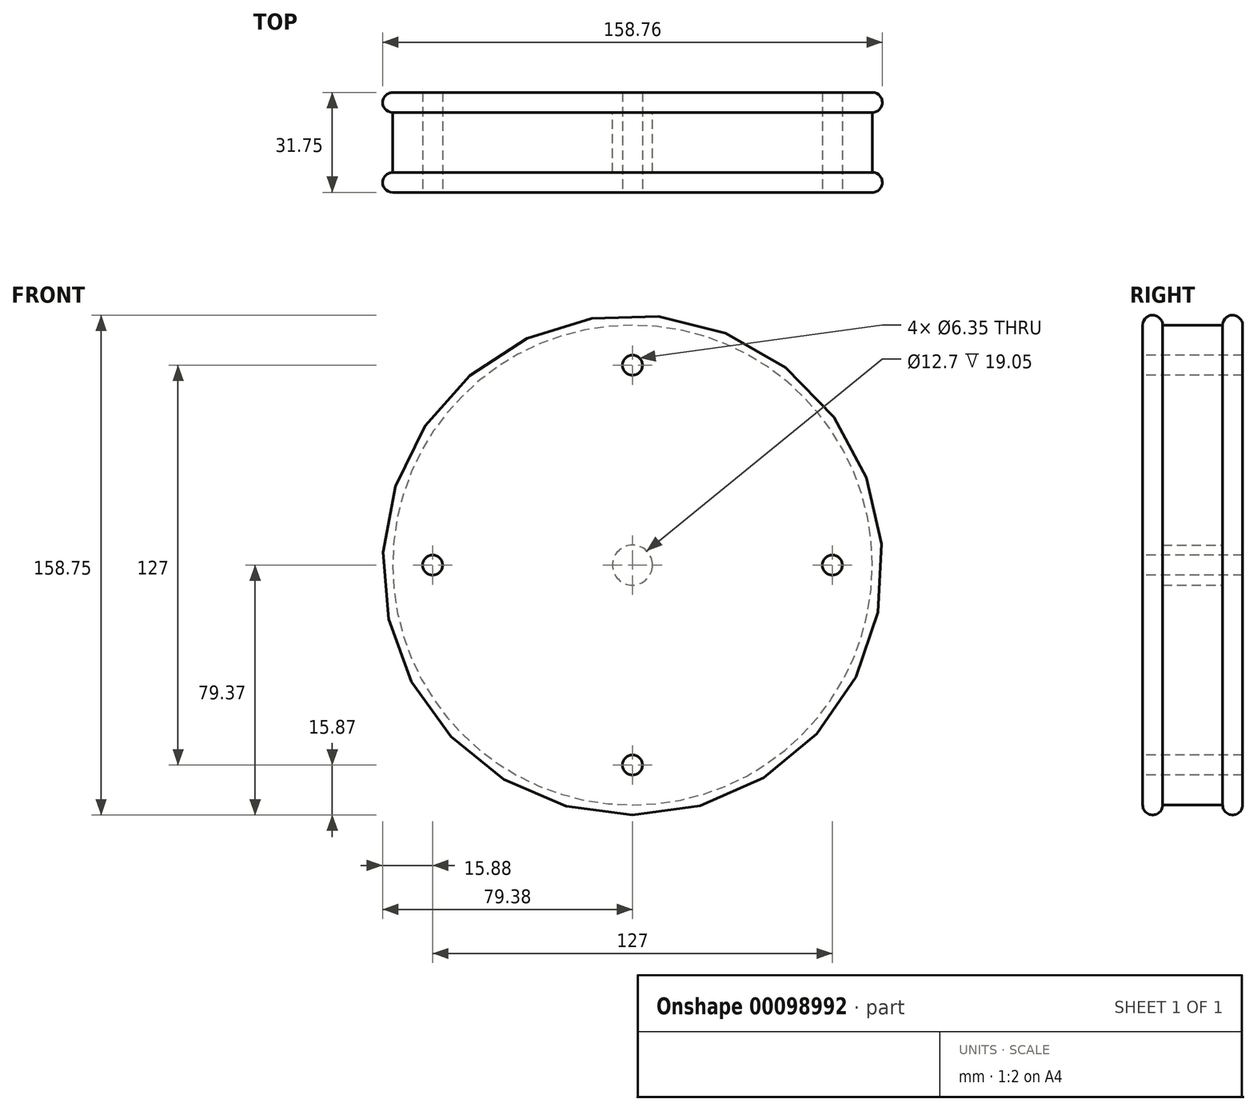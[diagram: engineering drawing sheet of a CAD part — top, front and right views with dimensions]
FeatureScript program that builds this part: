
annotation { "Feature Type Name" : "Feature", "Feature Type Description" : "" }
export const myFeature = defineFeature(function(context is Context, id is Id, definition is map)
    precondition{}
    {
        {
            var Q0;
            Q0=qCreatedBy(makeId("Front.planeOp"),FACE);
            var sketch = newSketch(context, id + "F0", { "sketchPlane" : qUnion([Q0])});
            skCircle(sketch, "E0", {"center": v(0, 0) * mm, "radius": 76.2 * mm});
            skCircle(sketch, "E1", {"center": v(0, 0) * mm, "radius": 6.35 * mm});
            skSolve(sketch);
        }
        {
            var Q0;
            Q0=makeQuery(id+"F0.imprint","IMPRINT",FACE,{"disambiguationData":[TD([[makeQuery(id+"F0.imprint","IMPRINT",EDGE,{"derivedFrom":sQuery(id+"F0.wireOp",EDGE,"E0")}),1.0]])]});
            extrude(context, id + "F1", {"entities" : qUnion([Q0]), "depth" : 25.4 * mm});
        }
        {
            var Q0;
            Q0=makeQuery(id+"F1.opExtrude","CAP_FACE",FACE,{"disambiguationData":[OSD([sQuery(id+"F0.wireOp",EDGE,"E0"),sQuery(id+"F0.wireOp",EDGE,"E1")])],"isStart":false});
            var sketch = newSketch(context, id + "F2", { "sketchPlane" : qUnion([Q0])});
            skCircle(sketch, "E2", {"center": v(0, 0) * mm, "radius": 79.38 * mm});
            skSolve(sketch);
        }
        {
            var Q0;
            Q0 = qSketchRegion(id + "F2", true);
            extrude(context, id + "F3", {"entities" : qUnion([Q0]), "operationType" : NewBodyOperationType.ADD, "oppositeDirection" : true, "depth" : 6.35 * mm});
        }
        {
            var Q0;
            Q0=makeQuery(id+"F0.imprint","IMPRINT",FACE,{"disambiguationData":[TD([[makeQuery(id+"F0.imprint","IMPRINT",EDGE,{"derivedFrom":sQuery(id+"F0.wireOp",EDGE,"E0")}),1.0]])]});
            var sketch = newSketch(context, id + "F4", { "sketchPlane" : qUnion([Q0])});
            skCircle(sketch, "E3", {"center": v(0, 0) * mm, "radius": 79.38 * mm});
            skSolve(sketch);
        }
        {
            var Q0;
            Q0 = qSketchRegion(id + "F4", true);
            extrude(context, id + "F5", {"entities" : qUnion([Q0]), "operationType" : NewBodyOperationType.ADD, "oppositeDirection" : true, "depth" : 6.35 * mm});
        }
        {
            var Q0;
            Q0=makeQuery(id+"F5.opExtrude","CAP_EDGE",EDGE,{"disambiguationData":[OSD([sQuery(id+"F4.wireOp",EDGE,"E3")])],"isStart":false});
            var Q1;
            Q1=makeQuery(id+"F5.opExtrude","CAP_EDGE",EDGE,{"disambiguationData":[OSD([sQuery(id+"F4.wireOp",EDGE,"E3")])],"isStart":true});
            var Q2;
            Q2=makeQuery(id+"F3.opExtrude","CAP_EDGE",EDGE,{"disambiguationData":[OSD([sQuery(id+"F2.wireOp",EDGE,"E2")])],"isStart":false});
            var Q3;
            Q3=makeQuery(id+"F3.opExtrude","CAP_EDGE",EDGE,{"disambiguationData":[OSD([sQuery(id+"F2.wireOp",EDGE,"E2")])],"isStart":true});
            fillet(context, id + "F6", {"entities" : qUnion([Q0, Q1, Q2, Q3]), "radius" : 3.17 * mm, "tangentPropagation" : true, "allowEdgeOverflow" : false});
        }
        {
            var Q0;
            Q0=makeQuery(id+"F3.boolean.opBoolean","MERGE",FACE,{"derivedFrom":[makeQuery(id+"F1.opExtrude","CAP_FACE",FACE,{"disambiguationData":[OSD([sQuery(id+"F0.wireOp",EDGE,"E0"),sQuery(id+"F0.wireOp",EDGE,"E1")])],"isStart":false}),makeQuery(id+"F3.opExtrude","CAP_FACE",FACE,{"disambiguationData":[OSD([sQuery(id+"F2.wireOp",EDGE,"E2")])],"isStart":true})]});
            var sketch = newSketch(context, id + "F7", { "sketchPlane" : qUnion([Q0])});
            skPoint(sketch, "E4", {"position": v(0, 63.5) * mm});
            skPoint(sketch, "E5", {"position": v(0, -63.5) * mm});
            skPoint(sketch, "E6", {"position": v(-63.5, 0) * mm});
            skPoint(sketch, "E7", {"position": v(63.5, 0) * mm});
            skSolve(sketch);
        }
        {
            var Q0;
            Q0=sQuery(id+"F7.wireOp",VERTEX,"E4");
            var Q1;
            Q1=sQuery(id+"F7.wireOp",VERTEX,"E5");
            var Q2;
            Q2=sQuery(id+"F7.wireOp",VERTEX,"E6");
            var Q3;
            Q3=sQuery(id+"F7.wireOp",VERTEX,"E7");
            var Q4;
            Q4=makeQuery(id+"F1.opExtrude","SWEPT_BODY",BODY,{"disambiguationData":[OSD([sQuery(id+"F0.wireOp",EDGE,"E0"),sQuery(id+"F0.wireOp",EDGE,"E1")])]});
            hole(context, id + "F8", {"style" : HoleStyle.SIMPLE, "endStyle" : HoleEndStyle.THROUGH, "holeDiameter" : 6.35 * mm, "locations" : qUnion([Q0, Q1, Q2, Q3]), "scope" : qUnion([Q4]), "isTappedThrough" : true});
        }
    });
